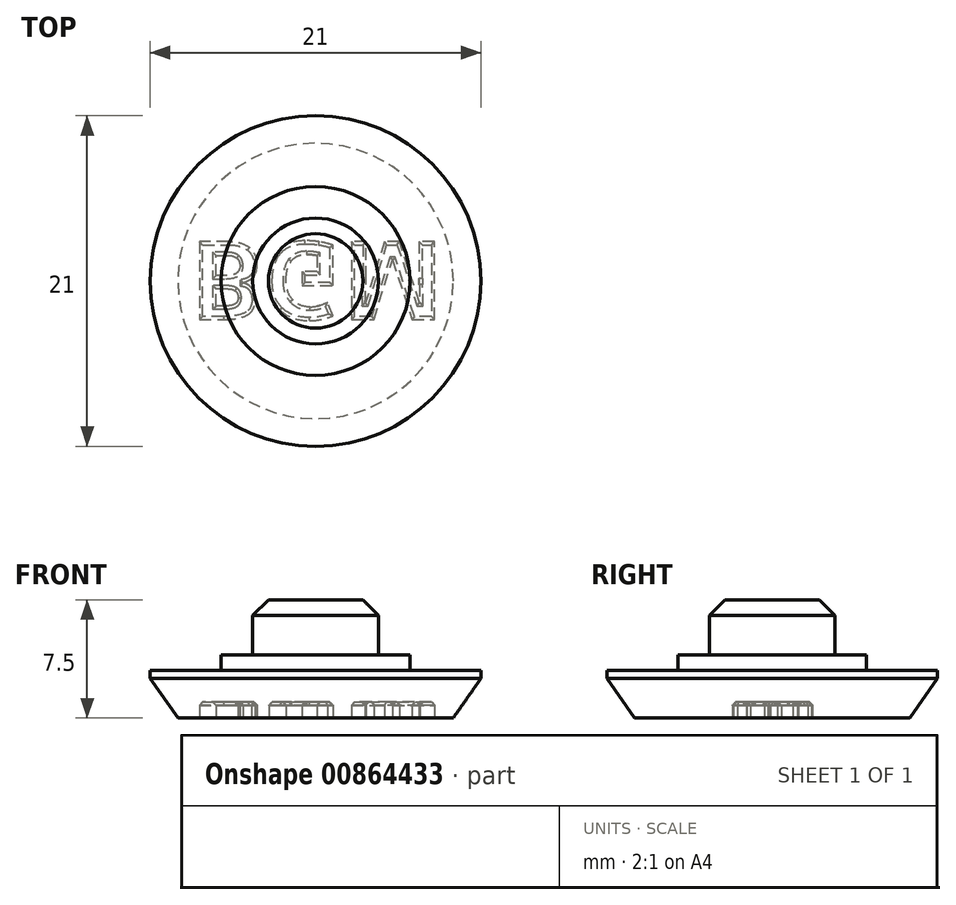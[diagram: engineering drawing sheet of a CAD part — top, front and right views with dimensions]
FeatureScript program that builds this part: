
annotation { "Feature Type Name" : "Feature", "Feature Type Description" : "" }
export const myFeature = defineFeature(function(context is Context, id is Id, definition is map)
    precondition{}
    {
        {
            var Q0;
            Q0=qCreatedBy(makeId("Top.planeOp"),FACE);
            var sketch = newSketch(context, id + "F0", { "sketchPlane" : qUnion([Q0])});
            skCircle(sketch, "E0", {"center": v(0, 0) * mm, "radius": 4 * mm});
            skCircle(sketch, "E1", {"center": v(0, 0) * mm, "radius": 10.5 * mm});
            skCircle(sketch, "E2", {"center": v(0, 0) * mm, "radius": 6 * mm});
            skSolve(sketch);
        }
        {
            var Q0;
            Q0=makeQuery(id+"F0.imprint","IMPRINT",FACE,{"disambiguationData":[TD([[makeQuery(id+"F0.imprint","IMPRINT",EDGE,{"derivedFrom":sQuery(id+"F0.wireOp",EDGE,"E1")}),1.0]])]});
            extrude(context, id + "F1", {"entities" : qUnion([Q0]), "depth" : 3 * mm, "offsetDistance" : 25 * mm});
        }
        {
            var Q0;
            Q0=makeQuery(id+"F0.imprint","IMPRINT",FACE,{"disambiguationData":[TD([[makeQuery(id+"F0.imprint","IMPRINT",EDGE,{"derivedFrom":sQuery(id+"F0.wireOp",EDGE,"E0")}),-1.0]])]});
            extrude(context, id + "F2", {"entities" : qUnion([Q0]), "operationType" : NewBodyOperationType.ADD, "depth" : 4 * mm, "offsetDistance" : 25 * mm});
        }
        {
            var Q0;
            Q0=makeQuery(id+"F0.imprint","IMPRINT",FACE,{"disambiguationData":[TD([[makeQuery(id+"F0.imprint","IMPRINT",EDGE,{"derivedFrom":sQuery(id+"F0.wireOp",EDGE,"E0")}),1.0]])]});
            extrude(context, id + "F3", {"entities" : qUnion([Q0]), "operationType" : NewBodyOperationType.ADD, "depth" : 7.5 * mm, "offsetDistance" : 25 * mm});
        }
        {
            var Q0;
            Q0=makeQuery(id+"F3.opExtrude","CAP_EDGE",EDGE,{"disambiguationData":[OSD([sQuery(id+"F0.wireOp",EDGE,"E0")])],"isStart":false});
            chamfer(context, id + "F4", {"entities" : qUnion([Q0]), "width" : 1 * mm, "tangentPropagation" : true});
        }
        {
            var Q0;
            Q0=makeQuery(id+"F1.opExtrude","CAP_EDGE",EDGE,{"disambiguationData":[OSD([sQuery(id+"F0.wireOp",EDGE,"E1")])],"isStart":true});
            chamfer(context, id + "F5", {"entities" : qUnion([Q0]), "chamferType" : ChamferType.OFFSET_ANGLE, "width" : 2.5 * mm, "oppositeDirection" : false, "angle" : 35 * degree, "tangentPropagation" : true});
        }
        {
            var Q0;
            {var subQ0=sQuery(id+"F0.wireOp",EDGE,"E0");var subQ1=sQuery(id+"F0.wireOp",EDGE,"E2");Q0=makeQuery(id+"F3.boolean.opBoolean","MERGE",FACE,{"derivedFrom":[makeQuery(id+"F2.boolean.opBoolean","MERGE",FACE,{"derivedFrom":[makeQuery(id+"F1.opExtrude","CAP_FACE",FACE,{"disambiguationData":[OSD([sQuery(id+"F0.wireOp",EDGE,"E1"),subQ1])],"isStart":true}),makeQuery(id+"F2.opExtrude","CAP_FACE",FACE,{"disambiguationData":[OSD([subQ0,subQ1])],"isStart":true})]}),makeQuery(id+"F3.opExtrude","CAP_FACE",FACE,{"disambiguationData":[OSD([subQ0])],"isStart":true})]});}
            var sketch = newSketch(context, id + "F6", { "sketchPlane" : qUnion([Q0])});
            skText(sketch, "E3", { "text": "BGM", "fontName": "OpenSans-Bold.ttf"});
            skLineSegment(sketch, "E4", {"start": v(0, 2.49) * mm, "end": v(0, 0) * mm, "construction": true});
            skLineSegment(sketch, "E5", {"start": v(0, 0) * mm, "end": v(0, -2.49) * mm, "construction": true});
            const initialGuessF6  = {"E3": [-0.008, -0.00249, 1, 0, 0.00498]};
            skSetInitialGuess(sketch, initialGuessF6);
            skSolve(sketch);
        }
        {
            var Q0;
            Q0=makeQuery(id+"F6.imprint","IMPRINT",FACE,{"disambiguationData":[TD([[makeQuery(id+"F6.imprint","IMPRINT",EDGE,{"derivedFrom":sQuery(id+"F6.wireOp",EDGE,"E3.sketch_text.stroke-0")}),-1.0]])]});
            var Q1;
            Q1=makeQuery(id+"F6.imprint","IMPRINT",FACE,{"disambiguationData":[TD([[makeQuery(id+"F6.imprint","IMPRINT",EDGE,{"derivedFrom":sQuery(id+"F6.wireOp",EDGE,"E3.sketch_text.stroke-25")}),-1.0]])]});
            var Q2;
            Q2=makeQuery(id+"F6.imprint","IMPRINT",FACE,{"disambiguationData":[TD([[makeQuery(id+"F6.imprint","IMPRINT",EDGE,{"derivedFrom":sQuery(id+"F6.wireOp",EDGE,"E3.sketch_text.stroke-44")}),-1.0]])]});
            extrude(context, id + "F7", {"entities" : qUnion([Q0, Q1, Q2]), "operationType" : NewBodyOperationType.REMOVE, "oppositeDirection" : true, "depth" : 1 * mm, "offsetDistance" : 25 * mm});
        }
        {
            var Q0;
            Q0=makeQuery(id+"F7.boolean.opBoolean","COPY",FACE,{"derivedFrom":makeQuery(id+"F7.opExtrude","CAP_FACE",FACE,{"disambiguationData":[OSD([sQuery(id+"F6.wireOp",EDGE,"E3.sketch_text.stroke-0"),sQuery(id+"F6.wireOp",EDGE,"E3.sketch_text.stroke-1"),sQuery(id+"F6.wireOp",EDGE,"E3.sketch_text.stroke-2"),sQuery(id+"F6.wireOp",EDGE,"E3.sketch_text.stroke-3"),sQuery(id+"F6.wireOp",EDGE,"E3.sketch_text.stroke-4"),sQuery(id+"F6.wireOp",EDGE,"E3.sketch_text.stroke-5"),sQuery(id+"F6.wireOp",EDGE,"E3.sketch_text.stroke-6"),sQuery(id+"F6.wireOp",EDGE,"E3.sketch_text.stroke-7"),sQuery(id+"F6.wireOp",EDGE,"E3.sketch_text.stroke-8"),sQuery(id+"F6.wireOp",EDGE,"E3.sketch_text.stroke-9"),sQuery(id+"F6.wireOp",EDGE,"E3.sketch_text.stroke-10"),sQuery(id+"F6.wireOp",EDGE,"E3.sketch_text.stroke-11"),sQuery(id+"F6.wireOp",EDGE,"E3.sketch_text.stroke-12"),sQuery(id+"F6.wireOp",EDGE,"E3.sketch_text.stroke-13"),sQuery(id+"F6.wireOp",EDGE,"E3.sketch_text.stroke-14"),sQuery(id+"F6.wireOp",EDGE,"E3.sketch_text.stroke-15"),sQuery(id+"F6.wireOp",EDGE,"E3.sketch_text.stroke-16"),sQuery(id+"F6.wireOp",EDGE,"E3.sketch_text.stroke-17"),sQuery(id+"F6.wireOp",EDGE,"E3.sketch_text.stroke-18"),sQuery(id+"F6.wireOp",EDGE,"E3.sketch_text.stroke-19"),sQuery(id+"F6.wireOp",EDGE,"E3.sketch_text.stroke-20"),sQuery(id+"F6.wireOp",EDGE,"E3.sketch_text.stroke-21"),sQuery(id+"F6.wireOp",EDGE,"E3.sketch_text.stroke-22"),sQuery(id+"F6.wireOp",EDGE,"E3.sketch_text.stroke-23"),sQuery(id+"F6.wireOp",EDGE,"E3.sketch_text.stroke-24")])],"isStart":false})});
            var Q1;
            Q1=makeQuery(id+"F7.boolean.opBoolean","COPY",FACE,{"derivedFrom":makeQuery(id+"F7.opExtrude","CAP_FACE",FACE,{"disambiguationData":[OSD([sQuery(id+"F6.wireOp",EDGE,"E3.sketch_text.stroke-25"),sQuery(id+"F6.wireOp",EDGE,"E3.sketch_text.stroke-26"),sQuery(id+"F6.wireOp",EDGE,"E3.sketch_text.stroke-27"),sQuery(id+"F6.wireOp",EDGE,"E3.sketch_text.stroke-28"),sQuery(id+"F6.wireOp",EDGE,"E3.sketch_text.stroke-29"),sQuery(id+"F6.wireOp",EDGE,"E3.sketch_text.stroke-30"),sQuery(id+"F6.wireOp",EDGE,"E3.sketch_text.stroke-31"),sQuery(id+"F6.wireOp",EDGE,"E3.sketch_text.stroke-32"),sQuery(id+"F6.wireOp",EDGE,"E3.sketch_text.stroke-33"),sQuery(id+"F6.wireOp",EDGE,"E3.sketch_text.stroke-34"),sQuery(id+"F6.wireOp",EDGE,"E3.sketch_text.stroke-35"),sQuery(id+"F6.wireOp",EDGE,"E3.sketch_text.stroke-36"),sQuery(id+"F6.wireOp",EDGE,"E3.sketch_text.stroke-37"),sQuery(id+"F6.wireOp",EDGE,"E3.sketch_text.stroke-38"),sQuery(id+"F6.wireOp",EDGE,"E3.sketch_text.stroke-39"),sQuery(id+"F6.wireOp",EDGE,"E3.sketch_text.stroke-40"),sQuery(id+"F6.wireOp",EDGE,"E3.sketch_text.stroke-41"),sQuery(id+"F6.wireOp",EDGE,"E3.sketch_text.stroke-42"),sQuery(id+"F6.wireOp",EDGE,"E3.sketch_text.stroke-43")])],"isStart":false})});
            var Q2;
            Q2=makeQuery(id+"F7.boolean.opBoolean","COPY",FACE,{"derivedFrom":makeQuery(id+"F7.opExtrude","CAP_FACE",FACE,{"disambiguationData":[OSD([sQuery(id+"F6.wireOp",EDGE,"E3.sketch_text.stroke-44"),sQuery(id+"F6.wireOp",EDGE,"E3.sketch_text.stroke-45"),sQuery(id+"F6.wireOp",EDGE,"E3.sketch_text.stroke-46"),sQuery(id+"F6.wireOp",EDGE,"E3.sketch_text.stroke-47"),sQuery(id+"F6.wireOp",EDGE,"E3.sketch_text.stroke-48"),sQuery(id+"F6.wireOp",EDGE,"E3.sketch_text.stroke-49"),sQuery(id+"F6.wireOp",EDGE,"E3.sketch_text.stroke-50"),sQuery(id+"F6.wireOp",EDGE,"E3.sketch_text.stroke-51"),sQuery(id+"F6.wireOp",EDGE,"E3.sketch_text.stroke-52"),sQuery(id+"F6.wireOp",EDGE,"E3.sketch_text.stroke-53"),sQuery(id+"F6.wireOp",EDGE,"E3.sketch_text.stroke-54"),sQuery(id+"F6.wireOp",EDGE,"E3.sketch_text.stroke-55"),sQuery(id+"F6.wireOp",EDGE,"E3.sketch_text.stroke-56"),sQuery(id+"F6.wireOp",EDGE,"E3.sketch_text.stroke-57"),sQuery(id+"F6.wireOp",EDGE,"E3.sketch_text.stroke-58"),sQuery(id+"F6.wireOp",EDGE,"E3.sketch_text.stroke-59"),sQuery(id+"F6.wireOp",EDGE,"E3.sketch_text.stroke-60"),sQuery(id+"F6.wireOp",EDGE,"E3.sketch_text.stroke-61"),sQuery(id+"F6.wireOp",EDGE,"E3.sketch_text.stroke-62")])],"isStart":false})});
            chamfer(context, id + "F8", {"entities" : qUnion([Q0, Q1, Q2]), "width" : 0.2 * mm, "tangentPropagation" : true});
        }
    });
